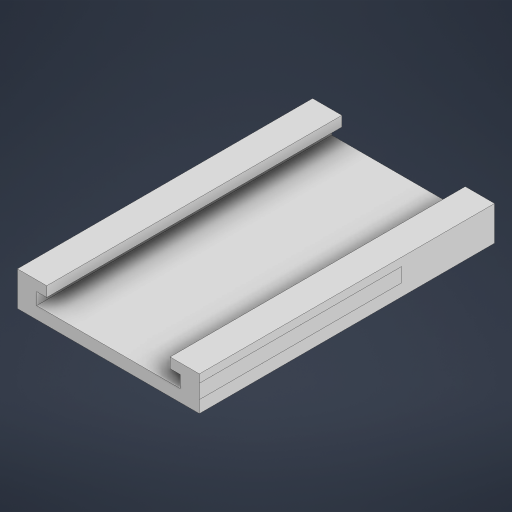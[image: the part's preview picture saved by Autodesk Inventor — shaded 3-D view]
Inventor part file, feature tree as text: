
AUTODESK INVENTOR PART (.ipt)
format: ipt  version: 2023 (Build 270158000, 158)  size: 281,600 bytes
history: native  units: mm
features: extrude x8, sketch x8
ambient origin geometry x8: Origin, YZ Plane, XZ Plane, XY Plane, X Axis, Y Axis, Z Axis, Center Point
bodies: Solid1 (feature_tree)
feature tree (16):
  extrude  "Extrusion1"  Depth=50.0mm
  extrude  "Extrusion2"  Depth=3.0mm
  extrude  "Extrusion3"  Depth=3.5mm TaperAngle=0.0deg
  extrude  "Extrusion4"  Depth=7.25mm
  extrude  "Extrusion5"  Depth=2.0mm TaperAngle=0.0deg
  extrude  "Extrusion6"  Depth=0.5mm TaperAngle=0.0deg
  extrude  "Extrusion7"  Depth=23.0mm TaperAngle=0.0deg
  extrude  "Extrusion8"  [1 undecoded]
  sketch  "Sketch1"  dims[d0=65.0mm d1=50.0mm]
  sketch  "Sketch2"  dims[d2=3.0mm d3=0.0mm d4=36.5mm]
  sketch  "Sketch3"  dims[d5=45.0mm d6=3.5mm d7=0.0mm]
  sketch  "Sketch4"  dims[d8=7.25mm d9=7.25mm]
  sketch  "Sketch5"  dims[d10=2.0mm d11=0.0mm d12=10.0mm d13=0.0mm]
  sketch  "Sketch6"  dims[d14=0.5mm d15=0.0mm d16=0.5mm d17=0.0mm]
  sketch  "Sketch7"  dims[d18=0.5mm d19=0.0mm d20=23.0mm d21=0.0mm]
  sketch  "Sketch8"
note: 1 required parameter value undecoded (feature->parameter linkage not recoverable at this tier; creation-order binding heuristic only, values carry confidence <= 0.55)
